# Revit family: IEK_Шина заземляющая главная_360х40х4мм_На 10 подключений_Медь
name_source: partatom
category: Обобщенные модели
units: mm (PartAtom-declared; Revit-internal decimal feet)

## family parameters
Может служить основой для арматурных стержней = Нет
Общий = Да
Основа = Грань
При загрузке вырезать с полостями = Нет
Размер круглого соединителя = Использовать диаметр
Тип детали = Нормальный
Точка расчета площади = Нет

## types (1)
- 360х40х4мм
    ADSK_URL страницы изделия = https://www.iek.ru
    ADSK_Версия Revit = 2019
    ADSK_Версия семейства = 1.0
    ADSK_Группирование = VIII. ЭЛЕМЕНТЫ ВНЕШНЕЙ МОЛНИЕЗАЩИТЫ
    ADSK_Единица измерения = шт
    ADSK_Завод-изготовитель = IEK
    ADSK_Код изделия = ZGB10-50-010-360
    ADSK_Масса = 0.946
    ADSK_Материал = Медь
    ADSK_Материал наименование = Медь
    ADSK_Наименование = Шина заземляющая главная 360х40х4мм на 10 подключений медь IEK
    ADSK_Ток = 630 А
    IEK_URL = https://www.iek.ru
    IEK_Описание = Шина заземляющая главная товарного знака IEK предназначена для объединения нулевых защитных и нулевые рабочих совмещенных проводников питающей линии; выводов контура заземления; заземляющих проводников; проводников системы уравнивания потенциалов. Закрепляется на пластиковых изоляторах.
    IEK_Цена за единицу = 5640
    KSI_CMa_Строительные материалы = СТ 10 12 20 10
    Отметка по умолчанию = 0 мм
